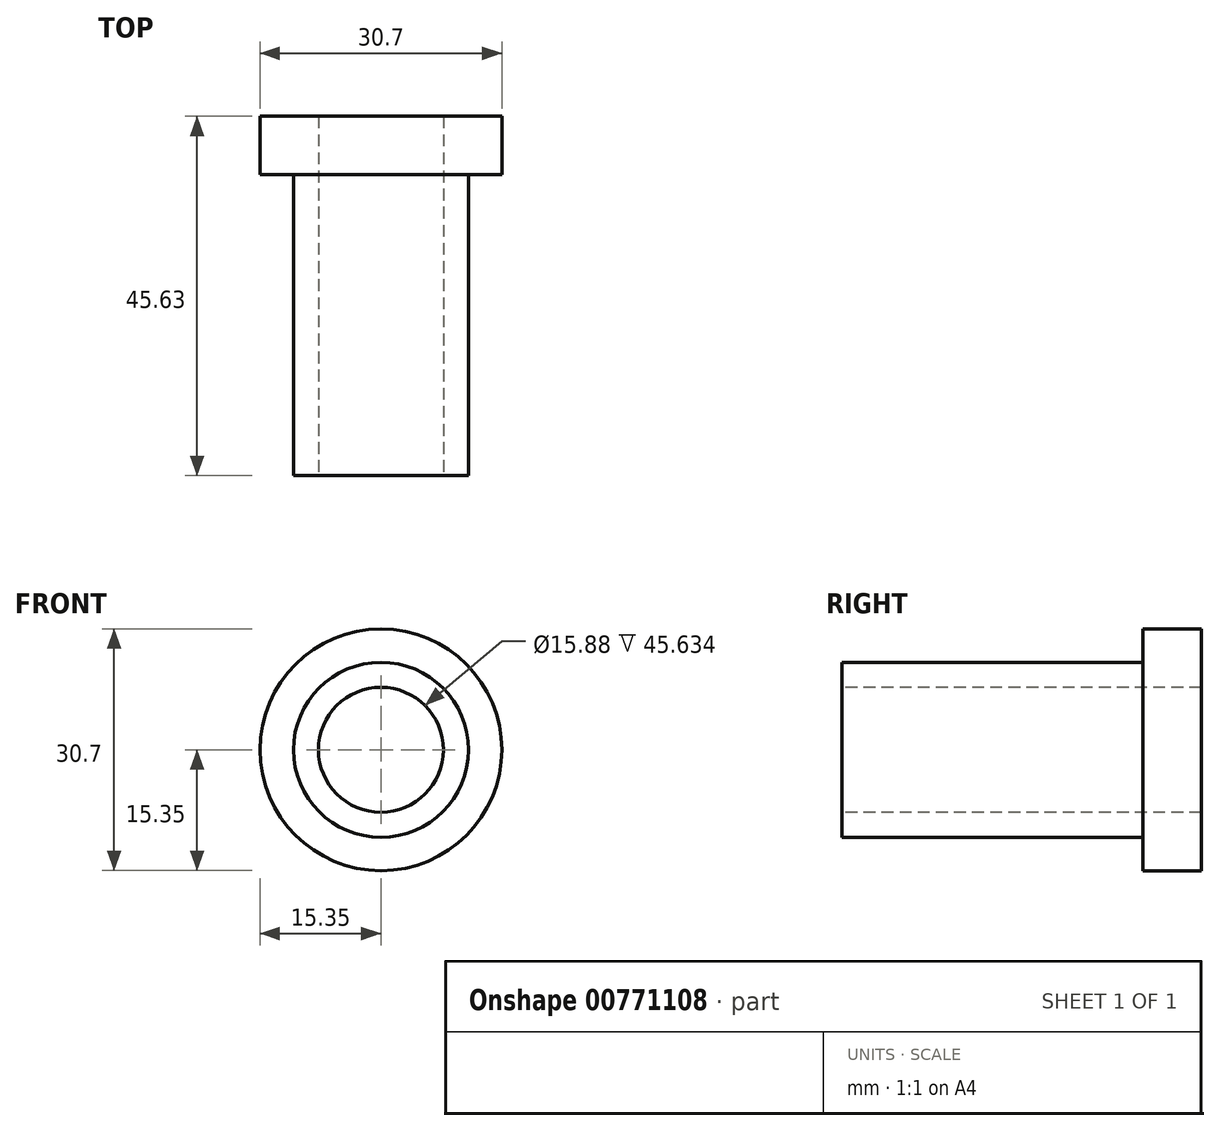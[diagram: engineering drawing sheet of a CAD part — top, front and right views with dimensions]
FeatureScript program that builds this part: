
annotation { "Feature Type Name" : "Feature", "Feature Type Description" : "" }
export const myFeature = defineFeature(function(context is Context, id is Id, definition is map)
    precondition{}
    {
        {
            var Q0;
            Q0=qCreatedBy(makeId("Right.planeOp"),FACE);
            var sketch = newSketch(context, id + "F0", { "sketchPlane" : qUnion([Q0])});
            skLineSegment(sketch, "E0", {"start": v(0, 0) * mm, "end": v(19.88, 0) * mm, "construction": true});
            skLineSegment(sketch, "E1", {"start": v(0, 7.94) * mm, "end": v(45.63, 7.94) * mm});
            skLineSegment(sketch, "E2", {"start": v(45.63, 7.94) * mm, "end": v(45.63, 15.35) * mm});
            skLineSegment(sketch, "E3", {"start": v(45.63, 15.35) * mm, "end": v(38.22, 15.35) * mm});
            skLineSegment(sketch, "E4", {"start": v(38.22, 15.35) * mm, "end": v(38.22, 11.11) * mm});
            skLineSegment(sketch, "E5", {"start": v(38.22, 11.11) * mm, "end": v(7.42, 11.11) * mm});
            skLineSegment(sketch, "E6", {"start": v(7.42, 11.11) * mm, "end": v(0, 11.11) * mm});
            skLineSegment(sketch, "E7", {"start": v(0, 11.11) * mm, "end": v(0, 7.94) * mm});
            skSolve(sketch);
        }
        {
            var Q0;
            Q0=qSketchRegion(id+"F0",true);
            var Q1;
            Q1=sQuery(id+"F0.wireOp",EDGE,"E0");
            revolve(context, id + "F1", {"surfaceOperationType" : NewSurfaceOperationType.NEW, "entities" : qUnion([Q0]), "axis" : qUnion([Q1]), "revolveType" : RevolveType.FULL});
        }
    });
